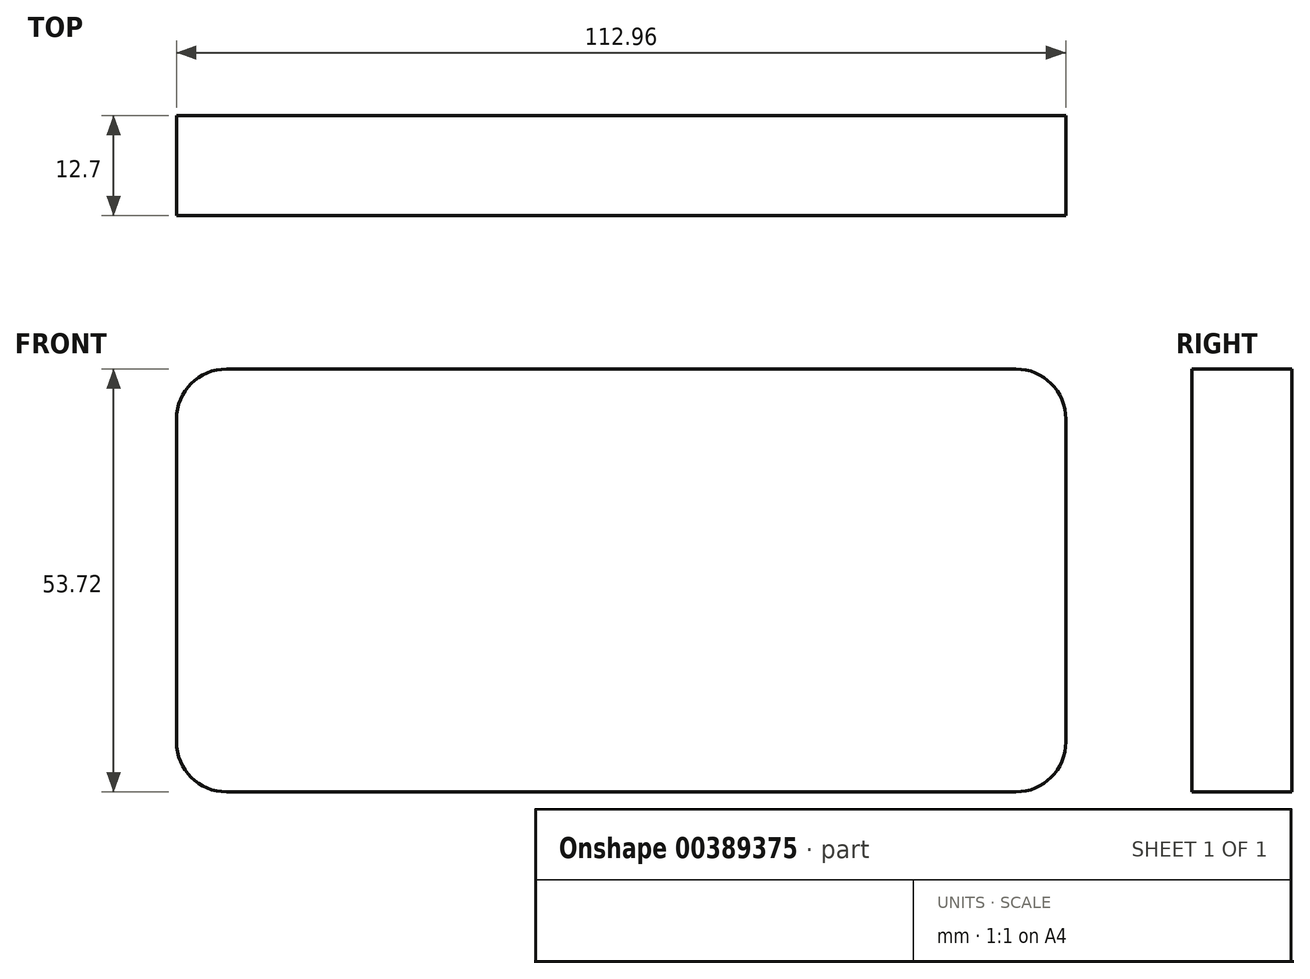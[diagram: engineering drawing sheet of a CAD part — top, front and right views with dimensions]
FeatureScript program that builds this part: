
annotation { "Feature Type Name" : "Feature", "Feature Type Description" : "" }
export const myFeature = defineFeature(function(context is Context, id is Id, definition is map)
    precondition{}
    {
        {
            var Q0;
            Q0=qCreatedBy(makeId("Front.planeOp"),FACE);
            var sketch = newSketch(context, id + "F0", { "sketchPlane" : qUnion([Q0])});
            skLineSegment(sketch, "E0.bottom", {"start": v(-17.46, 16.57) * mm, "end": v(82.8, 16.57) * mm});
            skLineSegment(sketch, "E0.top", {"start": v(-17.46, -37.15) * mm, "end": v(82.8, -37.15) * mm});
            skLineSegment(sketch, "E0.left", {"start": v(-23.81, 10.22) * mm, "end": v(-23.81, -30.8) * mm});
            skLineSegment(sketch, "E0.right", {"start": v(89.15, 10.22) * mm, "end": v(89.15, -30.8) * mm});
            skPoint(sketch, "E1.visualSharp", {"position": v(-23.81, 16.57) * mm});
            skArc(sketch, "E1.filletArc", {"start": v(-17.46, 16.57) * mm, "mid": v(-21.95, 14.71) * mm, "end": v(-23.81, 10.22) * mm});
            skPoint(sketch, "E2.visualSharp", {"position": v(-23.81, -37.15) * mm});
            skArc(sketch, "E2.filletArc", {"start": v(-23.81, -30.8) * mm, "mid": v(-21.95, -35.29) * mm, "end": v(-17.46, -37.15) * mm});
            skPoint(sketch, "E3.visualSharp", {"position": v(89.15, 16.57) * mm});
            skArc(sketch, "E3.filletArc", {"start": v(89.15, 10.22) * mm, "mid": v(87.3, 14.71) * mm, "end": v(82.8, 16.57) * mm});
            skPoint(sketch, "E4.visualSharp", {"position": v(89.15, -37.15) * mm});
            skArc(sketch, "E4.filletArc", {"start": v(82.8, -37.15) * mm, "mid": v(87.3, -35.29) * mm, "end": v(89.15, -30.8) * mm});
            skSolve(sketch);
        }
        {
            var Q0;
            Q0 = qSketchRegion(id + "F0", true);
            extrude(context, id + "F1", {"entities" : qUnion([Q0]), "depth" : 12.7 * mm});
        }
    });
